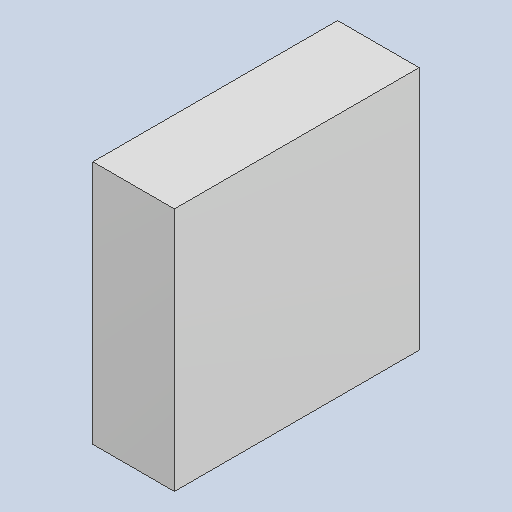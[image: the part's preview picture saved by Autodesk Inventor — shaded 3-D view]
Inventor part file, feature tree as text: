
AUTODESK INVENTOR PART (.ipt)
format: ipt  version: 2023.4 (Build 274418000, 418)  size: 81,408 bytes
history: native  units: mm
features: extrude x1
ambient origin geometry x8: Origin, YZ Plane, XZ Plane, XY Plane, X Axis, Y Axis, Z Axis, Center Point
bodies: Solid1 (feature_tree)
feature tree (1):
  extrude  "Extruded_35"  [1 undecoded]
note: 1 required parameter value undecoded (feature->parameter linkage not recoverable at this tier; creation-order binding heuristic only, values carry confidence <= 0.55)
